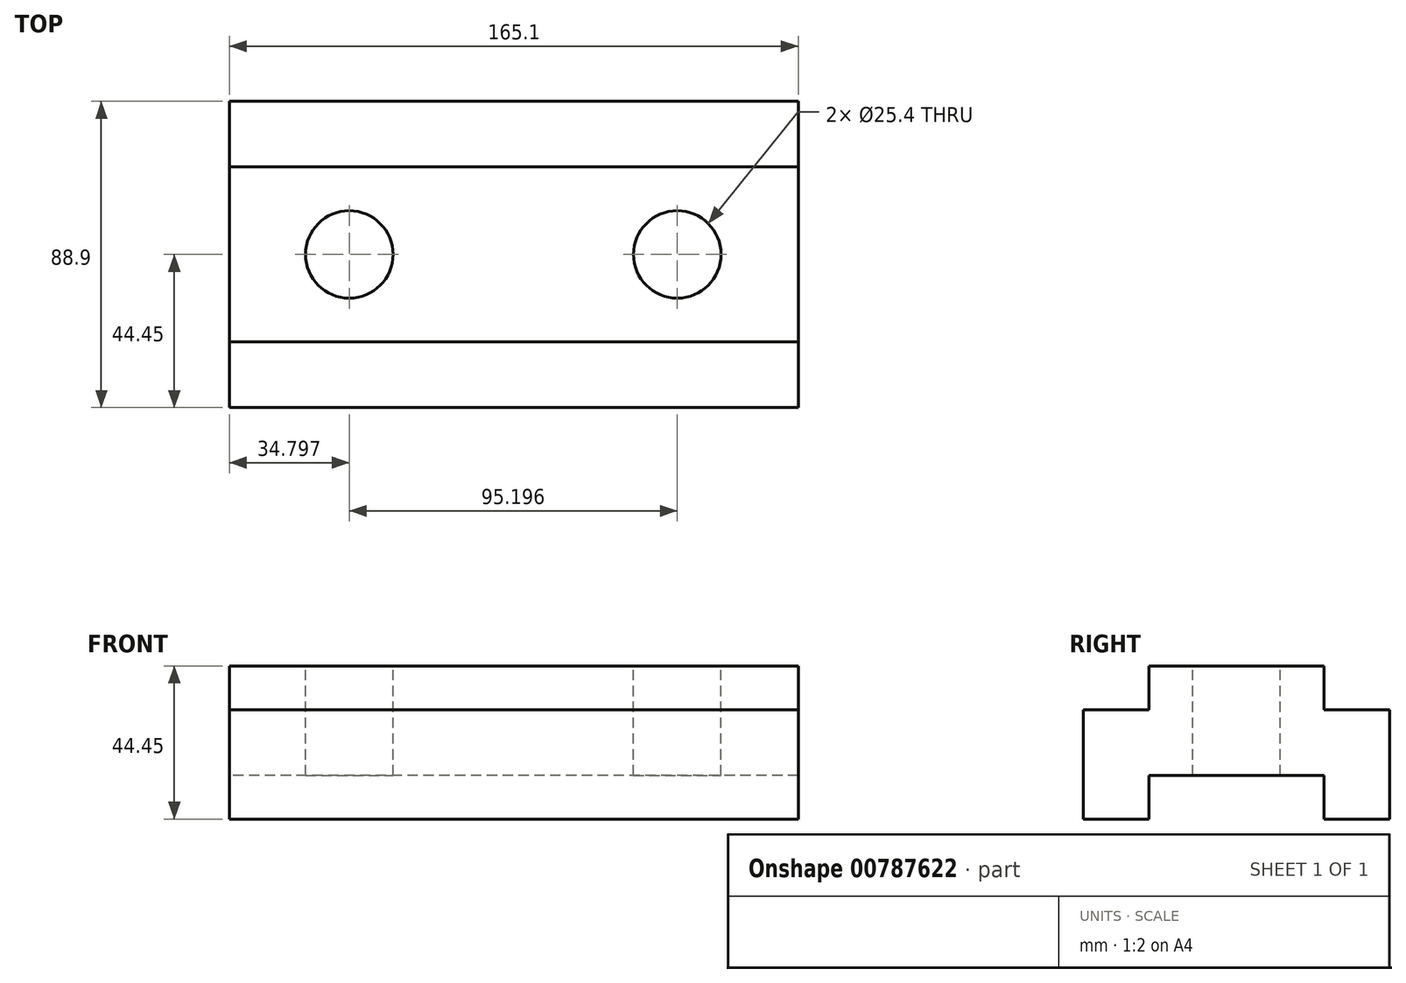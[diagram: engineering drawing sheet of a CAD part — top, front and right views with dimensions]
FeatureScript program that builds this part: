
annotation { "Feature Type Name" : "Feature", "Feature Type Description" : "" }
export const myFeature = defineFeature(function(context is Context, id is Id, definition is map)
    precondition{}
    {
        {
            var Q0;
            Q0=qCreatedBy(makeId("Right.planeOp"),FACE);
            var sketch = newSketch(context, id + "F0", { "sketchPlane" : qUnion([Q0])});
            skLineSegment(sketch, "E0", {"start": v(0, 0) * mm, "end": v(-25.4, 0) * mm});
            skLineSegment(sketch, "E1", {"start": v(0, 0) * mm, "end": v(25.4, 0) * mm});
            skLineSegment(sketch, "E2", {"start": v(25.4, 0) * mm, "end": v(25.4, -12.7) * mm});
            skLineSegment(sketch, "E3", {"start": v(-25.4, 0) * mm, "end": v(-25.4, -12.7) * mm});
            skLineSegment(sketch, "E4", {"start": v(-25.4, -12.7) * mm, "end": v(-44.45, -12.7) * mm});
            skLineSegment(sketch, "E5", {"start": v(-44.45, -12.7) * mm, "end": v(-44.45, 19.05) * mm});
            skLineSegment(sketch, "E6", {"start": v(-44.45, 19.05) * mm, "end": v(-25.4, 19.05) * mm});
            skLineSegment(sketch, "E7", {"start": v(-25.4, 19.05) * mm, "end": v(-25.4, 31.75) * mm});
            skLineSegment(sketch, "E8", {"start": v(-25.4, 31.75) * mm, "end": v(25.4, 31.75) * mm});
            skLineSegment(sketch, "E9", {"start": v(25.4, 31.75) * mm, "end": v(25.4, 19.05) * mm});
            skLineSegment(sketch, "E10", {"start": v(25.4, 19.05) * mm, "end": v(44.45, 19.05) * mm});
            skLineSegment(sketch, "E11", {"start": v(44.45, 19.05) * mm, "end": v(44.45, -12.7) * mm});
            skLineSegment(sketch, "E12", {"start": v(44.45, -12.7) * mm, "end": v(25.4, -12.7) * mm});
            skSolve(sketch);
        }
        {
            var Q0;
            Q0=makeQuery(id+"F0.imprint","IMPRINT",FACE,{"disambiguationData":[TD([[makeQuery(id+"F0.imprint","IMPRINT",EDGE,{"derivedFrom":sQuery(id+"F0.wireOp",EDGE,"E0")}),-1.0]])]});
            extrude(context, id + "F1", {"entities" : qUnion([Q0]), "depth" : 165.1 * mm, "offsetDistance" : 25.4 * mm});
        }
        {
            var Q0;
            Q0=makeQuery(id+"F1.opExtrude","SWEPT_FACE",FACE,{"disambiguationData":[OSD([sQuery(id+"F0.wireOp",EDGE,"E8")])]});
            var sketch = newSketch(context, id + "F2", { "sketchPlane" : qUnion([Q0])});
            skLineSegment(sketch, "E13", {"start": v(0, 0) * mm, "end": v(34.93, 0) * mm});
            skLineSegment(sketch, "E14", {"start": v(34.93, 0) * mm, "end": v(130.16, 0) * mm});
            skSolve(sketch);
        }
        {
            var Q0;
            {var subQ0=sQuery(id+"F0.wireOp",EDGE,"E8");Q0=makeQuery(id+"F2.imprint","IMPRINT",FACE,{"disambiguationData":[TD([[makeQuery(id+"F2.imprint","IMPRINT",EDGE,{"derivedFrom":makeQuery(id+"F1.opExtrude","CAP_EDGE",EDGE,{"disambiguationData":[OSD([subQ0])],"isStart":false})}),1.0]])]});}
            var sketch = newSketch(context, id + "F3", { "sketchPlane" : qUnion([Q0])});
            skCircle(sketch, "E15", {"center": v(34.8, 0) * mm, "radius": 12.7 * mm});
            skCircle(sketch, "E16", {"center": v(130, 0) * mm, "radius": 12.7 * mm});
            skSolve(sketch);
        }
        {
            var Q0;
            Q0=makeQuery(id+"F3.imprint","IMPRINT",FACE,{"disambiguationData":[TD([[makeQuery(id+"F3.imprint","IMPRINT",EDGE,{"derivedFrom":sQuery(id+"F3.wireOp",EDGE,"E15")}),1.0]])]});
            var Q1;
            Q1=makeQuery(id+"F3.imprint","IMPRINT",FACE,{"disambiguationData":[TD([[makeQuery(id+"F3.imprint","IMPRINT",EDGE,{"derivedFrom":sQuery(id+"F3.wireOp",EDGE,"E16")}),1.0]])]});
            extrude(context, id + "F4", {"entities" : qUnion([Q0, Q1]), "operationType" : NewBodyOperationType.REMOVE, "endBound" : BoundingType.THROUGH_ALL, "oppositeDirection" : true, "depth" : 25.4 * mm, "offsetDistance" : 25.4 * mm});
        }
    });
